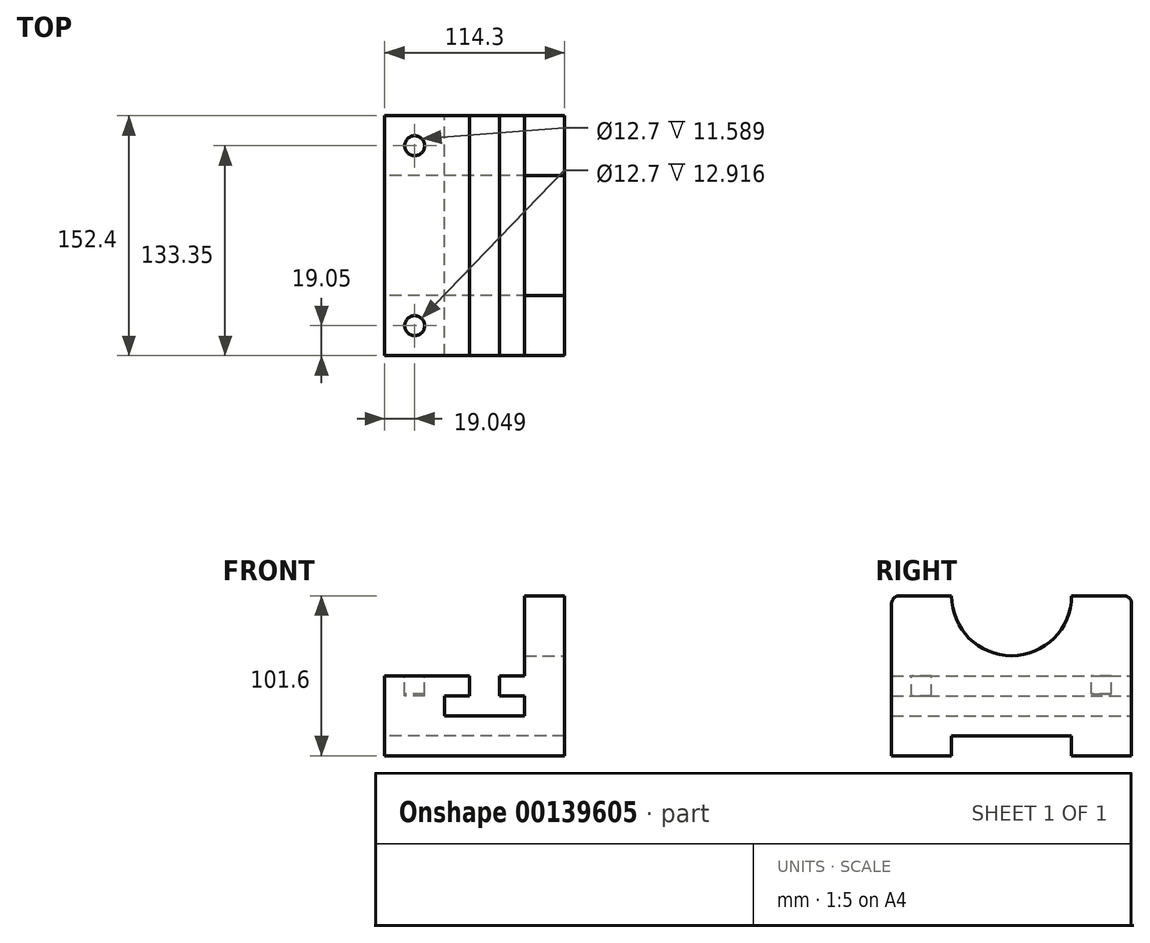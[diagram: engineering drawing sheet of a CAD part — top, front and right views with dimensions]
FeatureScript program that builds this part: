
annotation { "Feature Type Name" : "Feature", "Feature Type Description" : "" }
export const myFeature = defineFeature(function(context is Context, id is Id, definition is map)
    precondition{}
    {
        {
            var Q0;
            Q0=qCreatedBy(makeId("Front.planeOp"),FACE);
            var sketch = newSketch(context, id + "F0", { "sketchPlane" : qUnion([Q0])});
            skLineSegment(sketch, "E0", {"start": v(-71.42, 37.47) * mm, "end": v(-71.42, -13.33) * mm});
            skLineSegment(sketch, "E1", {"start": v(-71.42, 37.47) * mm, "end": v(-17.45, 37.47) * mm});
            skLineSegment(sketch, "E2", {"start": v(-17.45, 37.47) * mm, "end": v(-17.45, 24.77) * mm});
            skLineSegment(sketch, "E3", {"start": v(-17.45, 24.77) * mm, "end": v(-33.32, 24.77) * mm});
            skLineSegment(sketch, "E4", {"start": v(-33.32, 24.77) * mm, "end": v(-33.32, 12.07) * mm});
            skLineSegment(sketch, "E5", {"start": v(-33.32, 12.07) * mm, "end": v(17.48, 12.07) * mm});
            skLineSegment(sketch, "E6", {"start": v(17.48, 12.07) * mm, "end": v(17.48, 24.77) * mm});
            skLineSegment(sketch, "E7", {"start": v(17.48, 24.77) * mm, "end": v(1.6, 24.77) * mm});
            skLineSegment(sketch, "E8", {"start": v(1.6, 24.77) * mm, "end": v(1.6, 37.47) * mm});
            skLineSegment(sketch, "E9", {"start": v(1.6, 37.47) * mm, "end": v(17.48, 37.47) * mm});
            skLineSegment(sketch, "E10", {"start": v(17.48, 37.47) * mm, "end": v(17.48, 88.27) * mm});
            skLineSegment(sketch, "E11", {"start": v(17.48, 88.27) * mm, "end": v(42.88, 88.27) * mm});
            skLineSegment(sketch, "E12", {"start": v(42.88, 88.27) * mm, "end": v(42.88, -13.33) * mm});
            skLineSegment(sketch, "E13", {"start": v(-71.42, -13.33) * mm, "end": v(42.88, -13.33) * mm});
            skSolve(sketch);
        }
        {
            var Q0;
            Q0 = qSketchRegion(id + "F0", true);
            extrude(context, id + "F1", {"entities" : qUnion([Q0]), "depth" : 152.4 * mm});
        }
        {
            var Q0;
            Q0=makeQuery(id+"F1.opExtrude","SWEPT_FACE",FACE,{"disambiguationData":[OSD([sQuery(id+"F0.wireOp",EDGE,"E0")])]});
            var sketch = newSketch(context, id + "F2", { "sketchPlane" : qUnion([Q0])});
            skLineSegment(sketch, "E14", {"start": v(0, -13.33) * mm, "end": v(38.1, -13.33) * mm, "construction": true});
            skLineSegment(sketch, "E15", {"start": v(38.1, -13.33) * mm, "end": v(38.1, -0.63) * mm});
            skLineSegment(sketch, "E16", {"start": v(38.1, -0.63) * mm, "end": v(114.3, -0.63) * mm});
            skLineSegment(sketch, "E17", {"start": v(114.3, -0.63) * mm, "end": v(114.3, -13.33) * mm});
            skSolve(sketch);
        }
        {
            var Q0;
            {var subQ0=sQuery(id+"F2.wireOp",EDGE,"E15");Q0=makeQuery(id+"F2.imprint","IMPRINT",FACE,{"disambiguationData":[TD([[makeQuery(id+"F2.imprint","IMPRINT",EDGE,{"derivedFrom":subQ0}),-1.0]])]});}
            extrude(context, id + "F3", {"entities" : qUnion([Q0]), "operationType" : NewBodyOperationType.REMOVE, "oppositeDirection" : true, "depth" : 127 * mm});
        }
        {
            var Q0;
            Q0=makeQuery(id+"F1.opExtrude","SWEPT_FACE",FACE,{"disambiguationData":[OSD([sQuery(id+"F0.wireOp",EDGE,"E1")])]});
            var sketch = newSketch(context, id + "F4", { "sketchPlane" : qUnion([Q0])});
            skLineSegment(sketch, "E18", {"start": v(-52.37, 0) * mm, "end": v(-52.37, -19.05) * mm, "construction": true});
            skLineSegment(sketch, "E19", {"start": v(-52.37, -19.05) * mm, "end": v(-71.42, -19.05) * mm, "construction": true});
            skCircle(sketch, "E20", {"center": v(-52.37, -19.05) * mm, "radius": 6.35 * mm});
            skLineSegment(sketch, "E21", {"start": v(-52.37, -152.4) * mm, "end": v(-52.37, -133.35) * mm, "construction": true});
            skLineSegment(sketch, "E22", {"start": v(-52.37, -133.35) * mm, "end": v(-71.42, -133.35) * mm, "construction": true});
            skCircle(sketch, "E23", {"center": v(-52.37, -133.35) * mm, "radius": 6.35 * mm});
            skSolve(sketch);
        }
        {
            var Q0;
            Q0=makeQuery(id+"F4.imprint","IMPRINT",FACE,{"disambiguationData":[TD([[makeQuery(id+"F4.imprint","IMPRINT",EDGE,{"derivedFrom":sQuery(id+"F4.wireOp",EDGE,"E20")}),1.0]])]});
            extrude(context, id + "F5", {"entities" : qUnion([Q0]), "operationType" : NewBodyOperationType.REMOVE, "oppositeDirection" : true, "depth" : 11.6 * mm});
        }
        {
            var Q0;
            Q0=makeQuery(id+"F4.imprint","IMPRINT",FACE,{"disambiguationData":[TD([[makeQuery(id+"F4.imprint","IMPRINT",EDGE,{"derivedFrom":sQuery(id+"F4.wireOp",EDGE,"E23")}),1.0]])]});
            extrude(context, id + "F6", {"entities" : qUnion([Q0]), "operationType" : NewBodyOperationType.REMOVE, "oppositeDirection" : true, "depth" : 12.92 * mm});
        }
        {
            var Q0;
            Q0=makeQuery(id+"F1.opExtrude","SWEPT_FACE",FACE,{"disambiguationData":[OSD([sQuery(id+"F0.wireOp",EDGE,"E12")])]});
            var sketch = newSketch(context, id + "F7", { "sketchPlane" : qUnion([Q0])});
            skLineSegment(sketch, "E24", {"start": v(-152.4, 88.27) * mm, "end": v(-114.3, 88.27) * mm, "construction": true});
            skLineSegment(sketch, "E25", {"start": v(0, 88.27) * mm, "end": v(-38.1, 88.27) * mm, "construction": true});
            skCircle(sketch, "E26", {"center": v(-76.2, 88.27) * mm, "radius": 38.1 * mm});
            skSolve(sketch);
        }
        {
            var Q0;
            Q0 = qSketchRegion(id + "F7", true);
            extrude(context, id + "F8", {"entities" : qUnion([Q0]), "operationType" : NewBodyOperationType.REMOVE, "oppositeDirection" : true, "depth" : 25.4 * mm});
        }
        {
            var Q0;
            Q0=makeQuery(id+"F1.opExtrude","CAP_EDGE",EDGE,{"disambiguationData":[OSD([sQuery(id+"F0.wireOp",EDGE,"E11")])],"isStart":true});
            var Q1;
            Q1=makeQuery(id+"F1.opExtrude","CAP_EDGE",EDGE,{"disambiguationData":[OSD([sQuery(id+"F0.wireOp",EDGE,"E11")])],"isStart":false});
            fillet(context, id + "F9", {"entities" : qUnion([Q0, Q1]), "radius" : 5.08 * mm, "tangentPropagation" : true, "allowEdgeOverflow" : false});
        }
    });
